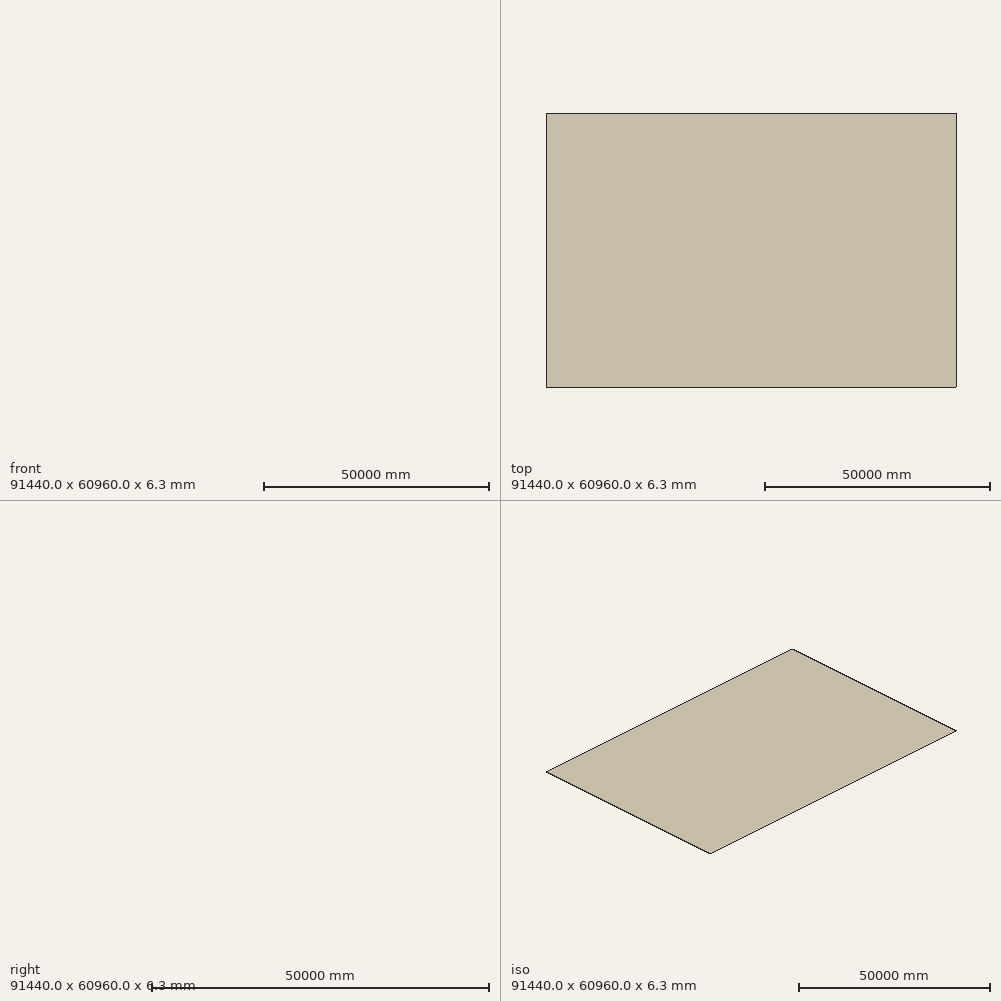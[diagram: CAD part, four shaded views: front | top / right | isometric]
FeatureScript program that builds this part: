
annotation { "Feature Type Name" : "Feature", "Feature Type Description" : "" }
export const myFeature = defineFeature(function(context is Context, id is Id, definition is map)
    precondition{}
    {
        {
            var Q0;
            Q0=qCreatedBy(makeId("Top.planeOp"),FACE);
            var sketch = newSketch(context, id + "F0", { "sketchPlane" : qUnion([Q0])});
            skLineSegment(sketch, "E0.bottom", {"start": v(0, 0) * mm, "end": v(91440, 0) * mm});
            skLineSegment(sketch, "E0.top", {"start": v(0, -60960) * mm, "end": v(91440, -60960) * mm});
            skLineSegment(sketch, "E0.left", {"start": v(0, 0) * mm, "end": v(0, -60960) * mm});
            skLineSegment(sketch, "E0.right", {"start": v(91440, 0) * mm, "end": v(91440, -60960) * mm});
            skSolve(sketch);
        }
        {
            var Q0;
            Q0=makeQuery(id+"F0.imprint","IMPRINT",FACE,{"disambiguationData":[TD([[makeQuery(id+"F0.imprint","IMPRINT",EDGE,{"derivedFrom":sQuery(id+"F0.wireOp",EDGE,"E0.bottom")}),-1.0]])]});
            extrude(context, id + "F1", {"entities" : qUnion([Q0]), "depth" : 6.35 * mm});
        }
    });
